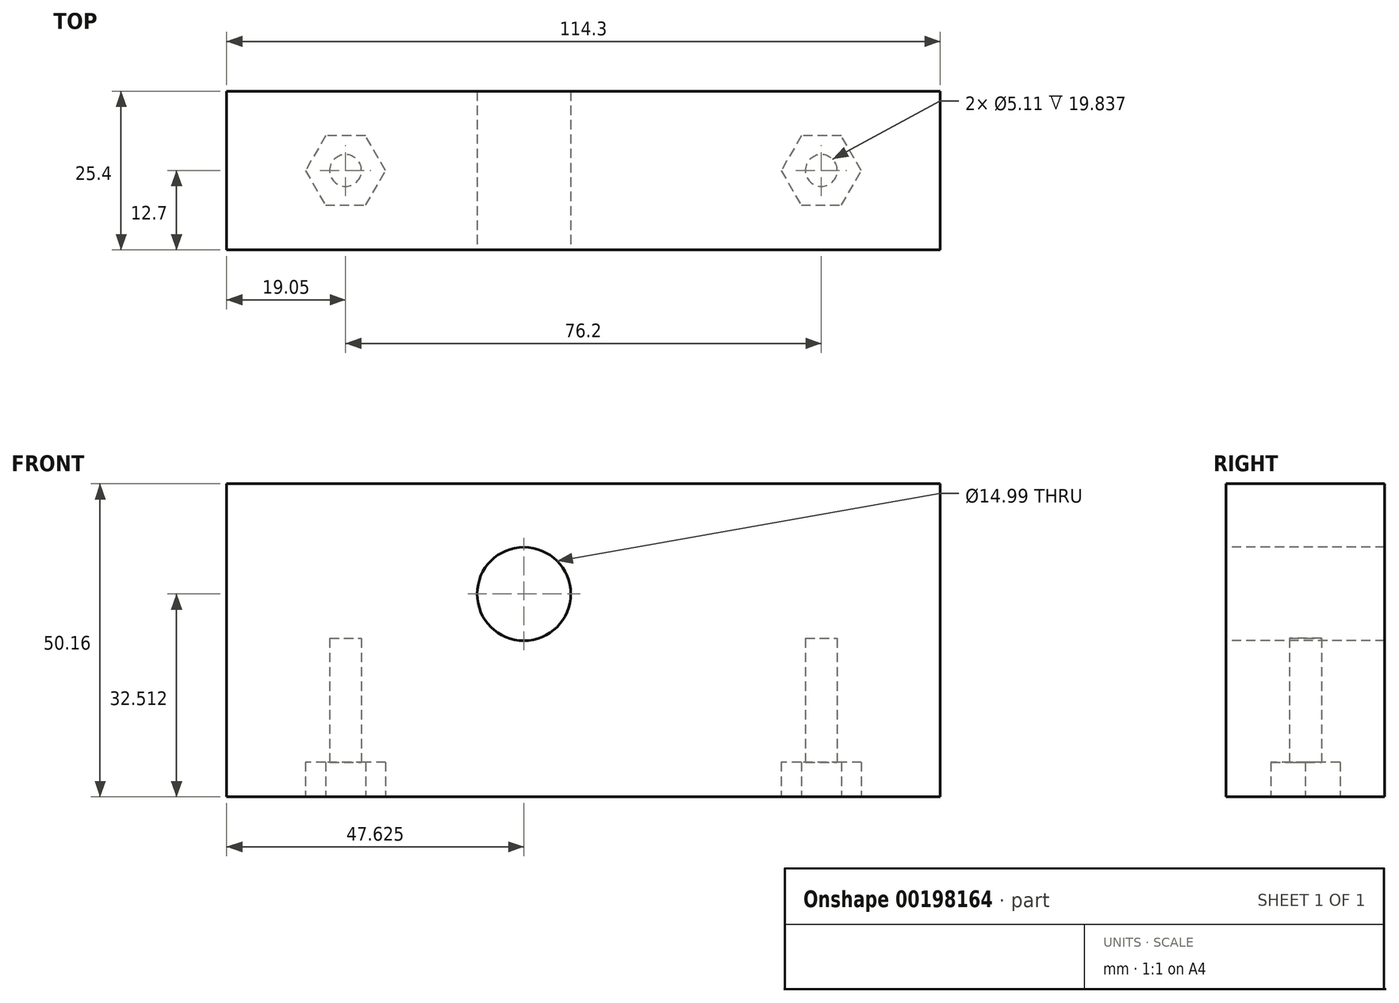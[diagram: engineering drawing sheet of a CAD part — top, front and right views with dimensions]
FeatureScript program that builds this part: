
annotation { "Feature Type Name" : "Feature", "Feature Type Description" : "" }
export const myFeature = defineFeature(function(context is Context, id is Id, definition is map)
    precondition{}
    {
        {
            var Q0;
            Q0=qCreatedBy(makeId("Top.planeOp"),FACE);
            var sketch = newSketch(context, id + "F0", { "sketchPlane" : qUnion([Q0])});
            skLineSegment(sketch, "E0.bottom", {"start": v(0, 0) * mm, "end": v(114.3, 0) * mm});
            skLineSegment(sketch, "E0.top", {"start": v(0, 25.4) * mm, "end": v(114.3, 25.4) * mm});
            skLineSegment(sketch, "E0.left", {"start": v(0, 0) * mm, "end": v(0, 25.4) * mm});
            skLineSegment(sketch, "E0.right", {"start": v(114.3, 0) * mm, "end": v(114.3, 25.4) * mm});
            skSolve(sketch);
        }
        {
            var Q0;
            Q0 = qSketchRegion(id + "F0", true);
            extrude(context, id + "F1", {"entities" : qUnion([Q0]), "depth" : 50.16 * mm});
        }
        {
            var Q0;
            Q0=makeQuery(id+"F1.opExtrude","SWEPT_FACE",FACE,{"disambiguationData":[OSD([sQuery(id+"F0.wireOp",EDGE,"E0.bottom")])]});
            var sketch = newSketch(context, id + "F2", { "sketchPlane" : qUnion([Q0])});
            skCircle(sketch, "E1", {"center": v(47.63, 32.51) * mm, "radius": 7.5 * mm});
            skSolve(sketch);
        }
        {
            var Q0;
            Q0 = qSketchRegion(id + "F2", true);
            extrude(context, id + "F3", {"entities" : qUnion([Q0]), "operationType" : NewBodyOperationType.REMOVE, "oppositeDirection" : true, "depth" : 25.4 * mm});
        }
        {
            var Q0;
            Q0=makeQuery(id+"F1.opExtrude","CAP_FACE",FACE,{"disambiguationData":[OSD([sQuery(id+"F0.wireOp",EDGE,"E0.bottom"),sQuery(id+"F0.wireOp",EDGE,"E0.top"),sQuery(id+"F0.wireOp",EDGE,"E0.left"),sQuery(id+"F0.wireOp",EDGE,"E0.right")])],"isStart":true});
            var sketch = newSketch(context, id + "F4", { "sketchPlane" : qUnion([Q0])});
            skCircle(sketch, "E2", {"center": v(19.05, -12.7) * mm, "radius": 2.55 * mm});
            skCircle(sketch, "E3", {"center": v(95.25, -12.7) * mm, "radius": 2.55 * mm});
            skSolve(sketch);
        }
        {
            var Q0;
            Q0 = qSketchRegion(id + "F4", true);
            extrude(context, id + "F5", {"entities" : qUnion([Q0]), "operationType" : NewBodyOperationType.REMOVE, "oppositeDirection" : true, "depth" : 25.4 * mm});
        }
        {
            var Q0;
            Q0=makeQuery(id+"F1.opExtrude","CAP_FACE",FACE,{"disambiguationData":[OSD([sQuery(id+"F0.wireOp",EDGE,"E0.bottom"),sQuery(id+"F0.wireOp",EDGE,"E0.top"),sQuery(id+"F0.wireOp",EDGE,"E0.left"),sQuery(id+"F0.wireOp",EDGE,"E0.right")])],"isStart":true});
            var sketch = newSketch(context, id + "F6", { "sketchPlane" : qUnion([Q0])});
            skCircle(sketch, "E4.cCircle", {"center": v(19.05, -12.7) * mm, "radius": 5.56 * mm, "construction": true});
            skLineSegment(sketch, "E4.0", {"start": v(15.84, -18.26) * mm, "end": v(12.63, -12.7) * mm});
            skLineSegment(sketch, "E4.1", {"start": v(12.63, -12.7) * mm, "end": v(15.84, -7.14) * mm});
            skLineSegment(sketch, "E4.2", {"start": v(15.84, -7.14) * mm, "end": v(22.26, -7.14) * mm});
            skLineSegment(sketch, "E4.3", {"start": v(22.26, -7.14) * mm, "end": v(25.47, -12.7) * mm});
            skLineSegment(sketch, "E4.4", {"start": v(25.47, -12.7) * mm, "end": v(22.26, -18.26) * mm});
            skLineSegment(sketch, "E4.5", {"start": v(22.26, -18.26) * mm, "end": v(15.84, -18.26) * mm});
            skPoint(sketch, "E4.0.midPoint", {"position": v(14.24, -15.48) * mm});
            skCircle(sketch, "E5.cCircle", {"center": v(95.25, -12.7) * mm, "radius": 5.56 * mm, "construction": true});
            skLineSegment(sketch, "E5.0", {"start": v(92.04, -18.26) * mm, "end": v(88.83, -12.7) * mm});
            skLineSegment(sketch, "E5.1", {"start": v(88.83, -12.7) * mm, "end": v(92.04, -7.14) * mm});
            skLineSegment(sketch, "E5.2", {"start": v(92.04, -7.14) * mm, "end": v(98.46, -7.14) * mm});
            skLineSegment(sketch, "E5.3", {"start": v(98.46, -7.14) * mm, "end": v(101.67, -12.7) * mm});
            skLineSegment(sketch, "E5.4", {"start": v(101.67, -12.7) * mm, "end": v(98.46, -18.26) * mm});
            skLineSegment(sketch, "E5.5", {"start": v(98.46, -18.26) * mm, "end": v(92.04, -18.26) * mm});
            skPoint(sketch, "E5.0.midPoint", {"position": v(90.44, -15.48) * mm});
            skSolve(sketch);
        }
        {
            var Q0;
            Q0 = qSketchRegion(id + "F6", true);
            extrude(context, id + "F7", {"entities" : qUnion([Q0]), "operationType" : NewBodyOperationType.REMOVE, "oppositeDirection" : true, "depth" : 5.56 * mm});
        }
    });
